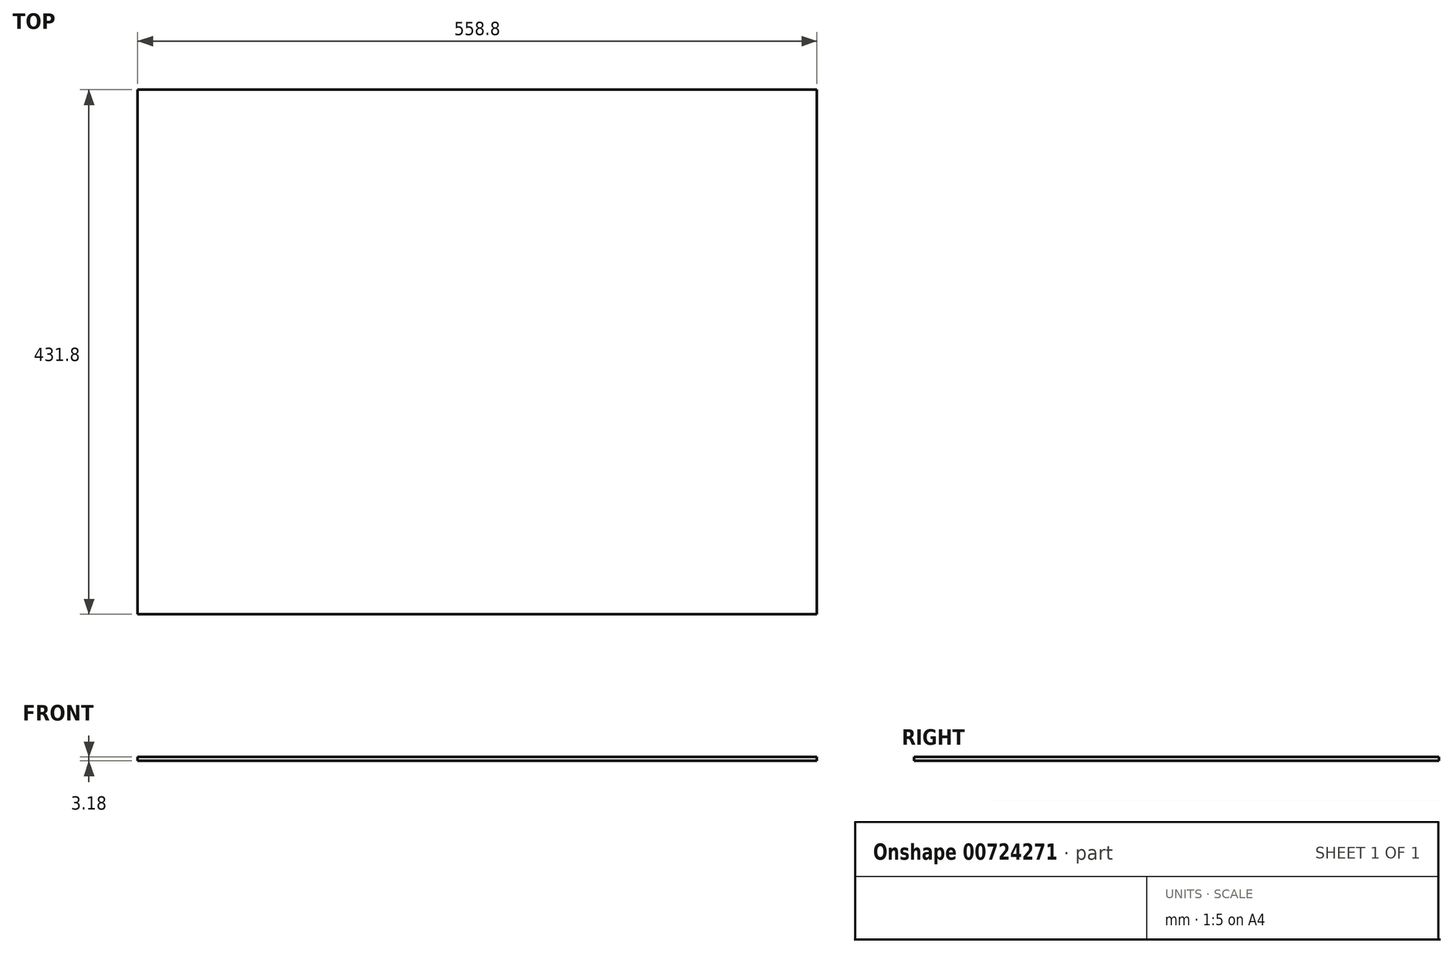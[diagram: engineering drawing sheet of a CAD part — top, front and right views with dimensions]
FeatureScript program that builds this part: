
annotation { "Feature Type Name" : "Feature", "Feature Type Description" : "" }
export const myFeature = defineFeature(function(context is Context, id is Id, definition is map)
    precondition{}
    {
        {
            var Q0;
            Q0=qCreatedBy(makeId("Top.planeOp"),FACE);
            var sketch = newSketch(context, id + "F0", { "sketchPlane" : qUnion([Q0])});
            skLineSegment(sketch, "E0.bottom", {"start": v(279.4, 215.9) * mm, "end": v(-279.4, 215.9) * mm});
            skLineSegment(sketch, "E0.top", {"start": v(279.4, -215.9) * mm, "end": v(-279.4, -215.9) * mm});
            skLineSegment(sketch, "E0.left", {"start": v(279.4, 215.9) * mm, "end": v(279.4, -215.9) * mm});
            skLineSegment(sketch, "E0.right", {"start": v(-279.4, 215.9) * mm, "end": v(-279.4, -215.9) * mm});
            skPoint(sketch, "E0.middle", {"position": v(0, 0) * mm});
            skSolve(sketch);
        }
        {
            var Q0;
            Q0 = qSketchRegion(id + "F0", true);
            extrude(context, id + "F1", {"entities" : qUnion([Q0]), "endBound" : BoundingType.SYMMETRIC, "depth" : 3.17 * mm, "offsetDistance" : 25.4 * mm});
        }
    });
